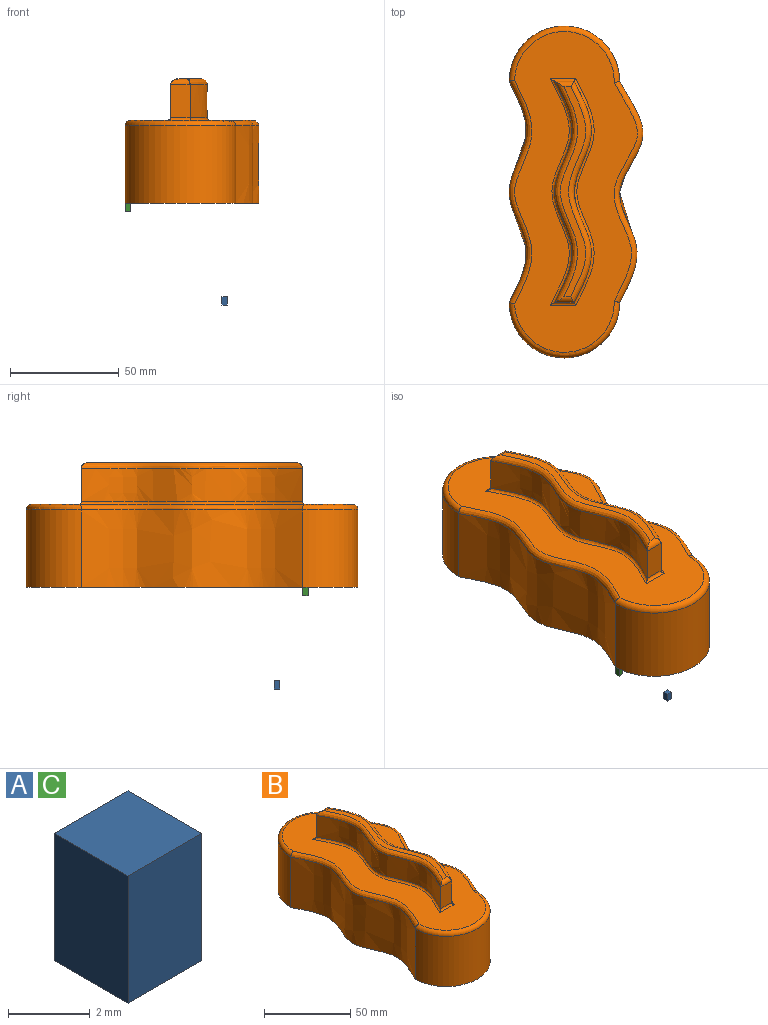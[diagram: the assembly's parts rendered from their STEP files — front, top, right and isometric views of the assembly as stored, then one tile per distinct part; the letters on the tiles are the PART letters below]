
ASSEMBLY  parts=3 mates=1
PART A: 6 faces, bbox 2.5x2.5x3.8 mm
  f0: plane 3.81x2.54mm, normal (0,1,0), area 9.7mm2, adj f1,f3,f4,f5
  f1: plane 3.81x2.54mm, normal (-1,0,0), area 9.7mm2, adj f0,f2,f4,f5
  f2: plane 3.81x2.54mm, normal (0,-1,0), area 9.7mm2, adj f1,f3,f4,f5
  f3: plane 3.81x2.54mm, normal (1,0,0), area 9.7mm2, adj f0,f2,f4,f5
  f4: plane 2.54x2.54mm, normal (0,0,-1), area 6.5mm2, adj f0,f1,f2,f3
  f5: plane 2.54x2.54mm, normal (0,0,1), area 6.5mm2, adj f0,f1,f2,f3
PART B: 23 faces, bbox 64.3x156.6x57.2 mm
  f0: cylinder r=25.4mm len=50.8mm, axis (0,0,-1), area 2837.6mm2, adj f1,f3,f5,f19
  f1: extruded ~101.6x35.56mm, area 3894mm2, adj f0,f2,f5,f21
  f2: cylinder r=25.4mm len=50.8mm, axis (0,0,-1), area 2837.6mm2, adj f1,f3,f5,f22
  f3: extruded ~101.6x35.56mm, area 3818.9mm2, adj f0,f2,f5,f20
  f4: plane 147.32x56.41mm, normal (0,0,1), area 5116.8mm2, adj f11,f12,f13,f14,f19,f20,f21,f22
  f5: plane 152.4x62.75mm, normal (0,0,-1), area 7259.8mm2, adj f0,f1,f2,f3
  f6: plane 96.55x11.77mm, normal (0,0,1), area 341.6mm2, adj f15,f16,f17,f18
  f7: plane 15.24x8.89mm, normal (0,1,0), area 135.5mm2, adj f8,f10,f14,f17
  f8: extruded ~101.6x15.24mm, area 1637mm2, adj f7,f9,f13,f15
  f9: plane 15.24x8.89mm, normal (0,-1,0), area 135.5mm2, adj f8,f10,f11,f16
  f10: extruded ~101.6x15.24mm, area 1637mm2, adj f7,f9,f12,f18
  f11: cylinder r=1.27mm len=11.76mm, axis (1,0,0), area 20.6mm2, adj f4,f9,f12,f13
  f12: bspline ~116.24x13.91mm, area 216.7mm2, adj f4,f10,f11,f14
  f13: bspline ~108.83x11.24mm, area 217.5mm2, adj f4,f8,f11,f14
  f14: cylinder r=1.27mm len=11.76mm, axis (-1,0,0), area 20.6mm2, adj f4,f7,f12,f13
  f15: bspline ~111.48x13.01mm, area 415.4mm2, adj f6,f8,f16,f17
  f16: cylinder r=2.54mm len=8.89mm, axis (-1,0,0), area 24.1mm2, adj f6,f9,f15,f18
  f17: cylinder r=2.54mm len=8.89mm, axis (1,0,0), area 24.1mm2, adj f6,f7,f15,f18
  f18: bspline ~106.32x11.71mm, area 418.8mm2, adj f6,f10,f16,f17
  f19: torus R=22.86mm, axis (0,0,1), area 306.8mm2, adj f0,f4,f20,f21
  f20: bspline ~109.1x11.9mm, area 429.3mm2, adj f3,f4,f19,f22
  f21: bspline ~105.56x14.02mm, area 435.8mm2, adj f1,f4,f19,f22
  f22: torus R=22.86mm, axis (0,0,1), area 306.8mm2, adj f2,f4,f20,f21
PART C: same geometry as A
PLACE A t=(-63.89,-39.26,-7.52)mm
PLACE B t=(-84.25,-0.14,35.33)mm
PLACE C t=(-108.38,-52.21,35.33)mm
MATE fastened C.f5 <-> B.f5  axis (0,0,1) through (-109.65,-50.94,35.33)mm
